# Revit family: LTRE24-SURFACE
name_source: partatom
category: Lighting Fixtures
units: mm (PartAtom-declared; Revit-internal decimal feet)

## family parameters
Cut with Voids When Loaded = No
Host = Face
Light Source = Yes
Part Type = Normal
Room Calculation Point = No
Round Connector Dimension = Use Diameter
Shared = No

## types (18) — shared parameters
Apparent Load = 0 VA
Color Filter = 16777215
Default Elevation = 4' - 0"
Dimming Lamp Color Temperature Shift = <None>
Emit from Line Length = 2' - 0"
IES FILE LINK = http://www.columbialighting.com
LEGNTH = 4' - 6"
Manufacturer = COLUMBIA
Model = LTRE22
Number of Poles = 1
Power Factor = 1
Shield = Glass
Tilt Angle = 90.00°
Voltage = 0 V
WIDTH = 2' - 0"

## per-type parameters (varying)
| type | Photometric Web File | Product Page URL | Wattage Comments |
| LTRE22-30HLG-RFA-EU | 6811.ies | https://www.currentlighting.com | 40 |
| LTRE22-30LWG-RFA-EU | 6805.ies | https://www.currentlighting.com | 24 |
| LTRE22-30MLG-RFA-EU | 6808.ies | https://www.currentlighting.com | 30 |
| LTRE22-30VLG-RFA-EU | 6814.ies | https://www.currentlighting.com | 51 |
| LTRE22-35HLG-RFA-EU | 6812.ies | https://www.currentlighting.com | 40 |
| LTRE22-35LWG-RFA-EU | 6806.ies | https://www.currentlighting.com | 24 |
| LTRE22-35MLG-RFA-EU | 6809.ies | https://www.currentlighting.com | 30 |
| LTRE22-35VLG-RFA-EU | 6815.ies | https://www.currentlighting.com | 51 |
| LTRE22-40HLG-RFA-EU | 6813.ies | https://www.currentlighting.com | 40 |
| LTRE22-40LWG-RFA-EU | 6807.ies | https://www.currentlighting.com | 24 |
| LTRE22-40MLG-RFA-EU | 6807.ies | https://www.currentlighting.com | 24 |
| LTRE22-40VLG-RFA-EU | 6816.ies | http://www.columbialighting.com | 51 |
| LTRE24-30LWG-RFA-EU | 6823.ies | https://www.currentlighting.com | 40 |
| LTRE24-30MLG-RFA-ESD | 6826.ies | https://www.currentlighting.com | 51 |
| LTRE24-35LWG-RFA-EU | 6824.ies | https://www.currentlighting.com | 40 |
| LTRE24-35MLG-RFA-ESD | 6827.ies | https://www.currentlighting.com | 51 |
| LTRE24-40LWG-RFA-ESD | 6825.ies | https://www.currentlighting.com | 40 |
| LTRE24-40MLG-RFA-ESD | 6828.ies | https://www.currentlighting.com | 51 |

## geometry (parser evidence)
native form markers: Sweep x3
no freeform markers — native parametric forms only
